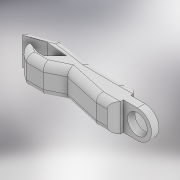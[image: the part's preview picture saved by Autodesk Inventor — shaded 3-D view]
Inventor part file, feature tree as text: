
AUTODESK INVENTOR PART (.ipt)
format: ipt  version: 2022 (Build 260153000, 153)  size: 243,200 bytes
history: native  units: mm
features: extrude x5, sketch x4, fillet x3, projected_geometry x3, plane x2, chamfer x1
ambient origin geometry x8: Origin, YZ Plane, XZ Plane, XY Plane, X Axis, Y Axis, Z Axis, Center Point
bodies: Body1 (feature_tree)
feature tree (18):
  extrude  "Extrusion1"  Depth=2.25mm
  plane  "Work Plane3"
  fillet  "Fillet5"  Radius=2.25mm
  sketch  "Sketch9"  dims[d38=4.25mm d39=8.5mm d40=0.0mm]
  extrude  "Extrusion6"  Depth=8.5mm TaperAngle=0.0deg
  extrude  "Extrusion7"  Depth=8.5mm TaperAngle=0.0deg
  plane  "Work Plane4"
  extrude  "Extrusion8"  Depth=8.5mm TaperAngle=0.0deg
  extrude  "Extrusion9"  Depth=2.0mm TaperAngle=45.0deg
  chamfer  "Chamfer3"  Distance=2.0mm
  fillet  "Fillet6"  Radius=2.0mm
  fillet  "Fillet7"  [1 undecoded]
  sketch  "Sketch4"  dims[d14=8.5mm d15=0.0mm d24=8.0mm d25=2.25mm]
  projected_geometry  "Projected Loop6"
  projected_geometry  "Projected Loop7"
  sketch  "Sketch10"  dims[d41=8.5mm d42=0.0mm d43=8.5mm d44=0.0mm]
  projected_geometry  "Projected Loop8"
  sketch  "Sketch11"  dims[d45=6.0mm d46=8.5mm d47=0.0mm d48=2.0mm d49=2.0mm d50=45.0deg d51=2.0mm d52=2.0mm]
note: 1 required parameter value undecoded (feature->parameter linkage not recoverable at this tier; creation-order binding heuristic only, values carry confidence <= 0.55)
